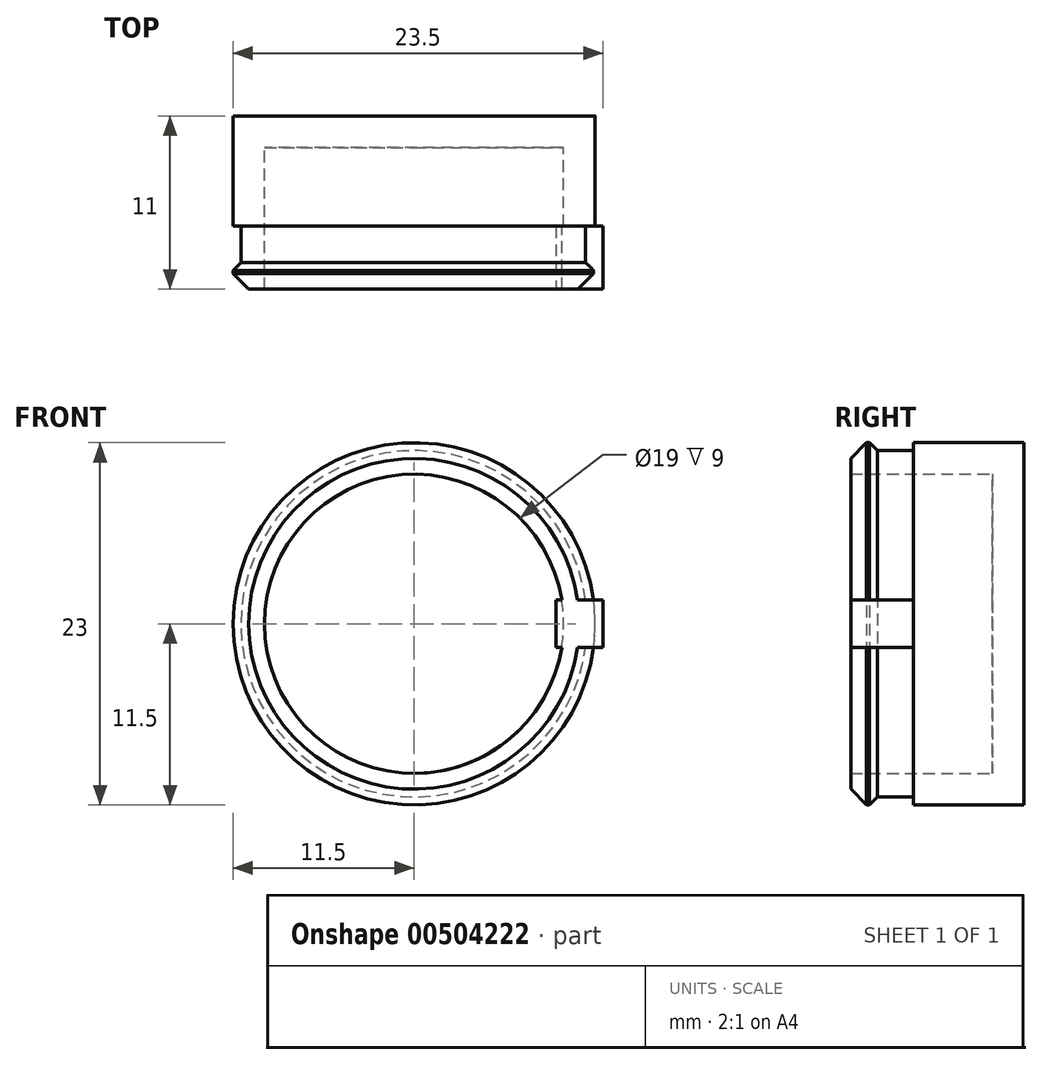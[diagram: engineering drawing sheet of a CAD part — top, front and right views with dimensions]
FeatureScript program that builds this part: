
annotation { "Feature Type Name" : "Feature", "Feature Type Description" : "" }
export const myFeature = defineFeature(function(context is Context, id is Id, definition is map)
    precondition{}
    {
        {
            var Q0;
            Q0=qCreatedBy(makeId("Front.planeOp"),FACE);
            var sketch = newSketch(context, id + "F0", { "sketchPlane" : qUnion([Q0])});
            skCircle(sketch, "E0", {"center": v(0, 0) * mm, "radius": 11.5 * mm});
            skCircle(sketch, "E1", {"center": v(0, 0) * mm, "radius": 9.5 * mm});
            skSolve(sketch);
        }
        {
            var Q0;
            Q0=makeQuery(id+"F0.imprint","IMPRINT",FACE,{"disambiguationData":[TD([[makeQuery(id+"F0.imprint","IMPRINT",EDGE,{"derivedFrom":sQuery(id+"F0.wireOp",EDGE,"E0")}),1.0]])]});
            extrude(context, id + "F1", {"entities" : qUnion([Q0]), "depth" : 7 * mm});
        }
        {
            var Q0;
            Q0=makeQuery(id+"F0.imprint","IMPRINT",FACE,{"disambiguationData":[TD([[makeQuery(id+"F0.imprint","IMPRINT",EDGE,{"derivedFrom":sQuery(id+"F0.wireOp",EDGE,"E1")}),1.0]])]});
            extrude(context, id + "F2", {"entities" : qUnion([Q0]), "operationType" : NewBodyOperationType.ADD, "depth" : 2 * mm});
        }
        {
            var Q0;
            Q0=makeQuery(id+"F1.opExtrude","CAP_FACE",FACE,{"disambiguationData":[OSD([sQuery(id+"F0.wireOp",EDGE,"E0"),sQuery(id+"F0.wireOp",EDGE,"E1")])],"isStart":false});
            var sketch = newSketch(context, id + "F3", { "sketchPlane" : qUnion([Q0])});
            skCircle(sketch, "E2", {"center": v(0, 0) * mm, "radius": 11 * mm});
            skCircle(sketch, "E3", {"center": v(0, 0) * mm, "radius": 9.5 * mm});
            skSolve(sketch);
        }
        {
            var Q0;
            Q0=makeQuery(id+"F3.imprint","IMPRINT",FACE,{"disambiguationData":[TD([[makeQuery(id+"F3.imprint","IMPRINT",EDGE,{"derivedFrom":sQuery(id+"F3.wireOp",EDGE,"E2")}),1.0]])]});
            extrude(context, id + "F4", {"entities" : qUnion([Q0]), "operationType" : NewBodyOperationType.ADD, "depth" : 2 * mm});
        }
        {
            var Q0;
            Q0=makeQuery(id+"F4.opExtrude","CAP_FACE",FACE,{"disambiguationData":[OSD([sQuery(id+"F3.wireOp",EDGE,"E2"),sQuery(id+"F3.wireOp",EDGE,"E3")])],"isStart":false});
            var sketch = newSketch(context, id + "F5", { "sketchPlane" : qUnion([Q0])});
            skCircle(sketch, "E4", {"center": v(0, 0) * mm, "radius": 11.5 * mm});
            skCircle(sketch, "E5", {"center": v(0, 0) * mm, "radius": 9.5 * mm});
            skSolve(sketch);
        }
        {
            var Q0;
            Q0=makeQuery(id+"F5.imprint","IMPRINT",FACE,{"disambiguationData":[TD([[makeQuery(id+"F5.imprint","IMPRINT",EDGE,{"derivedFrom":sQuery(id+"F5.wireOp",EDGE,"E5")}),-1.0]])]});
            var Q1;
            Q1=makeQuery(id+"F5.imprint","IMPRINT",FACE,{"disambiguationData":[TD([[makeQuery(id+"F5.imprint","IMPRINT",EDGE,{"derivedFrom":sQuery(id+"F5.wireOp",EDGE,"E4")}),1.0]])]});
            extrude(context, id + "F6", {"entities" : qUnion([Q0, Q1]), "operationType" : NewBodyOperationType.ADD, "depth" : 2 * mm});
        }
        {
            var Q0;
            Q0=makeQuery(id+"F6.opExtrude","CAP_EDGE",EDGE,{"disambiguationData":[OSD([sQuery(id+"F5.wireOp",EDGE,"E4")])],"isStart":true});
            chamfer(context, id + "F7", {"entities" : qUnion([Q0]), "width" : 0.8 * mm, "tangentPropagation" : true});
        }
        {
            var Q0;
            Q0=makeQuery(id+"F6.opExtrude","CAP_EDGE",EDGE,{"disambiguationData":[OSD([sQuery(id+"F5.wireOp",EDGE,"E4")])],"isStart":false});
            chamfer(context, id + "F8", {"entities" : qUnion([Q0]), "width" : 1 * mm, "tangentPropagation" : true});
        }
        {
            var Q0;
            Q0=makeQuery(id+"F6.opExtrude","CAP_FACE",FACE,{"disambiguationData":[OSD([sQuery(id+"F5.wireOp",EDGE,"E4"),sQuery(id+"F5.wireOp",EDGE,"E5")])],"isStart":false});
            var sketch = newSketch(context, id + "F9", { "sketchPlane" : qUnion([Q0])});
            skLineSegment(sketch, "E6.bottom", {"start": v(12, 1.5) * mm, "end": v(9, 1.5) * mm});
            skLineSegment(sketch, "E6.top", {"start": v(12, -1.5) * mm, "end": v(9, -1.5) * mm});
            skLineSegment(sketch, "E6.left", {"start": v(12, 1.5) * mm, "end": v(12, -1.5) * mm});
            skLineSegment(sketch, "E6.right", {"start": v(9, 1.5) * mm, "end": v(9, -1.5) * mm});
            skSolve(sketch);
        }
        {
            var Q0;
            Q0 = qSketchRegion(id + "F9", true);
            extrude(context, id + "F10", {"entities" : qUnion([Q0]), "operationType" : NewBodyOperationType.ADD, "oppositeDirection" : true, "depth" : 4 * mm, "offsetDistance" : 25 * mm});
        }
        {
            var Q0;
            Q0=qCreatedBy(makeId("Top.planeOp"),FACE);
            var sketch = newSketch(context, id + "F11", { "sketchPlane" : qUnion([Q0])});
            skLineSegment(sketch, "E7", {"start": v(0, 15.13) * mm, "end": v(0, -31.81) * mm});
            skSolve(sketch);
        }
    });
